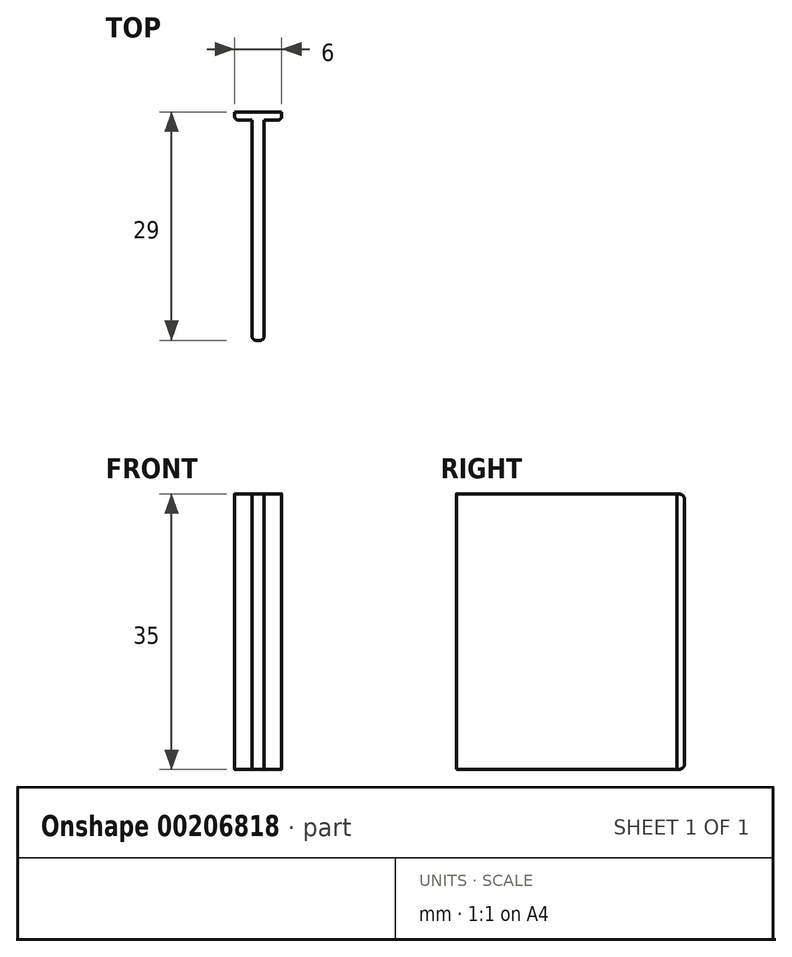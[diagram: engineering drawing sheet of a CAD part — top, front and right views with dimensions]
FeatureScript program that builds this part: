
annotation { "Feature Type Name" : "Feature", "Feature Type Description" : "" }
export const myFeature = defineFeature(function(context is Context, id is Id, definition is map)
    precondition{}
    {
        {
            var Q0;
            Q0=qCreatedBy(makeId("Front.planeOp"),FACE);
            var sketch = newSketch(context, id + "F0", { "sketchPlane" : qUnion([Q0])});
            skLineSegment(sketch, "E0.bottom", {"start": v(3, 17.5) * mm, "end": v(-3, 17.5) * mm});
            skLineSegment(sketch, "E0.top", {"start": v(3, -17.5) * mm, "end": v(-3, -17.5) * mm});
            skLineSegment(sketch, "E0.left", {"start": v(3, 17.5) * mm, "end": v(3, -17.5) * mm});
            skLineSegment(sketch, "E0.right", {"start": v(-3, 17.5) * mm, "end": v(-3, -17.5) * mm});
            skPoint(sketch, "E0.middle", {"position": v(0, 0) * mm});
            skLineSegment(sketch, "E1.bottom", {"start": v(0.75, 17.5) * mm, "end": v(-0.75, 17.5) * mm, "construction": true});
            skLineSegment(sketch, "E1.top", {"start": v(0.75, -17.5) * mm, "end": v(-0.75, -17.5) * mm, "construction": true});
            skLineSegment(sketch, "E1.left", {"start": v(0.75, 17.5) * mm, "end": v(0.75, -17.5) * mm});
            skLineSegment(sketch, "E1.right", {"start": v(-0.75, 17.5) * mm, "end": v(-0.75, -17.5) * mm});
            skSolve(sketch);
        }
        {
            var Q0;
            Q0=makeQuery(id+"F0.imprint","IMPRINT",FACE,{"disambiguationData":[TD([[makeQuery(id+"F0.imprint","IMPRINT",EDGE,{"derivedFrom":sQuery(id+"F0.wireOp",EDGE,"E0.bottom")}),1.0]])]});
            extrude(context, id + "F1", {"entities" : qUnion([Q0]), "oppositeDirection" : true, "depth" : 1 * mm});
        }
        {
            var Q0;
            {var subQ0=sQuery(id+"F0.wireOp",EDGE,"E1.left");Q0=makeQuery(id+"F0.imprint","IMPRINT",FACE,{"disambiguationData":[TD([[makeQuery(id+"F0.imprint","IMPRINT",EDGE,{"derivedFrom":subQ0}),-1.0]])]});}
            extrude(context, id + "F2", {"entities" : qUnion([Q0]), "operationType" : NewBodyOperationType.ADD, "depth" : 28 * mm});
        }
        {
            var Q0;
            Q0=makeQuery(id+"F1.opExtrude","CAP_EDGE",EDGE,{"disambiguationData":[OSD([sQuery(id+"F0.wireOp",EDGE,"E0.right")])],"isStart":true});
            var Q1;
            Q1=makeQuery(id+"F1.opExtrude","CAP_EDGE",EDGE,{"disambiguationData":[OSD([sQuery(id+"F0.wireOp",EDGE,"E0.left")])],"isStart":true});
            var Q2;
            Q2=makeQuery(id+"F2.opExtrude","CAP_EDGE",EDGE,{"disambiguationData":[OSD([sQuery(id+"F0.wireOp",EDGE,"E1.right")])],"isStart":false});
            var Q3;
            Q3=makeQuery(id+"F2.opExtrude","CAP_EDGE",EDGE,{"disambiguationData":[OSD([sQuery(id+"F0.wireOp",EDGE,"E1.left")])],"isStart":false});
            fillet(context, id + "F3", {"entities" : qUnion([Q0, Q1, Q2, Q3]), "radius" : .5 * mm, "tangentPropagation" : true, "allowEdgeOverflow" : false});
        }
        {
            var Q0;
            Q0=makeQuery(id+"F1.opExtrude","CAP_EDGE",EDGE,{"disambiguationData":[OSD([sQuery(id+"F0.wireOp",EDGE,"E0.bottom")])],"isStart":false});
            var Q1;
            Q1=makeQuery(id+"F1.opExtrude","CAP_EDGE",EDGE,{"disambiguationData":[OSD([sQuery(id+"F0.wireOp",EDGE,"E0.top")])],"isStart":false});
            fillet(context, id + "F4", {"entities" : qUnion([Q0, Q1]), "radius" : .75 * mm, "tangentPropagation" : true, "allowEdgeOverflow" : false});
        }
    });
